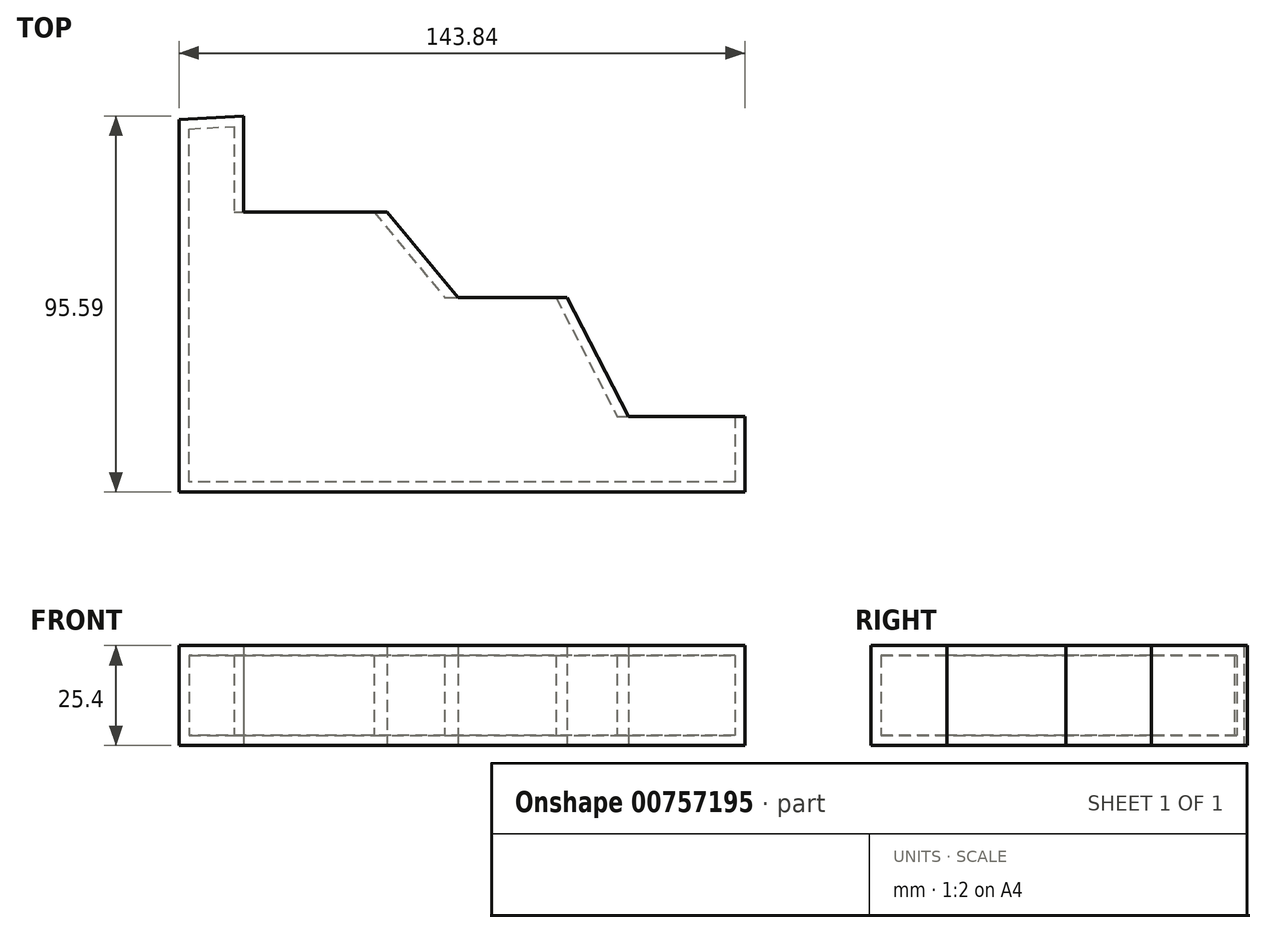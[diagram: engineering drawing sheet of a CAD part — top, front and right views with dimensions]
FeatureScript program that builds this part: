
annotation { "Feature Type Name" : "Feature", "Feature Type Description" : "" }
export const myFeature = defineFeature(function(context is Context, id is Id, definition is map)
    precondition{}
    {
        {
            var Q0;
            Q0=qCreatedBy(makeId("Top.planeOp"),FACE);
            var sketch = newSketch(context, id + "F0", { "sketchPlane" : qUnion([Q0])});
            skLineSegment(sketch, "E0", {"start": v(-60, 37.4) * mm, "end": v(-60, 12.98) * mm});
            skLineSegment(sketch, "E1", {"start": v(-60, 12.98) * mm, "end": v(-23.67, 12.98) * mm});
            skLineSegment(sketch, "E2", {"start": v(-23.67, 12.98) * mm, "end": v(-5.65, -8.7) * mm});
            skLineSegment(sketch, "E3", {"start": v(-5.65, -8.7) * mm, "end": v(22.14, -8.7) * mm});
            skLineSegment(sketch, "E4", {"start": v(22.14, -8.7) * mm, "end": v(37.71, -38.94) * mm});
            skLineSegment(sketch, "E5", {"start": v(37.71, -38.94) * mm, "end": v(67.34, -38.94) * mm});
            skLineSegment(sketch, "E6", {"start": v(67.34, -38.94) * mm, "end": v(67.34, -58.18) * mm});
            skLineSegment(sketch, "E7", {"start": v(67.34, -58.18) * mm, "end": v(-76.5, -58.18) * mm});
            skLineSegment(sketch, "E8", {"start": v(-76.5, -58.18) * mm, "end": v(-76.5, 36.5) * mm});
            skLineSegment(sketch, "E9", {"start": v(-76.5, 36.5) * mm, "end": v(-60, 37.4) * mm});
            skSolve(sketch);
        }
        {
            var Q0;
            Q0 = qSketchRegion(id + "F0", true);
            extrude(context, id + "F1", {"entities" : qUnion([Q0]), "depth" : 25.4 * mm, "offsetDistance" : 25.4 * mm});
        }
        {
            var Q0;
            Q0=makeQuery(id+"F1.opExtrude","SWEPT_FACE",FACE,{"disambiguationData":[OSD([sQuery(id+"F0.wireOp",EDGE,"E5")])]});
            var Q1;
            Q1=makeQuery(id+"F1.opExtrude","SWEPT_FACE",FACE,{"disambiguationData":[OSD([sQuery(id+"F0.wireOp",EDGE,"E3")])]});
            var Q2;
            Q2=makeQuery(id+"F1.opExtrude","SWEPT_FACE",FACE,{"disambiguationData":[OSD([sQuery(id+"F0.wireOp",EDGE,"E1")])]});
            shell(context, id + "F2", {"entities" : qUnion([Q0, Q1, Q2]), "thickness" : 2.54 * mm});
        }
    });
